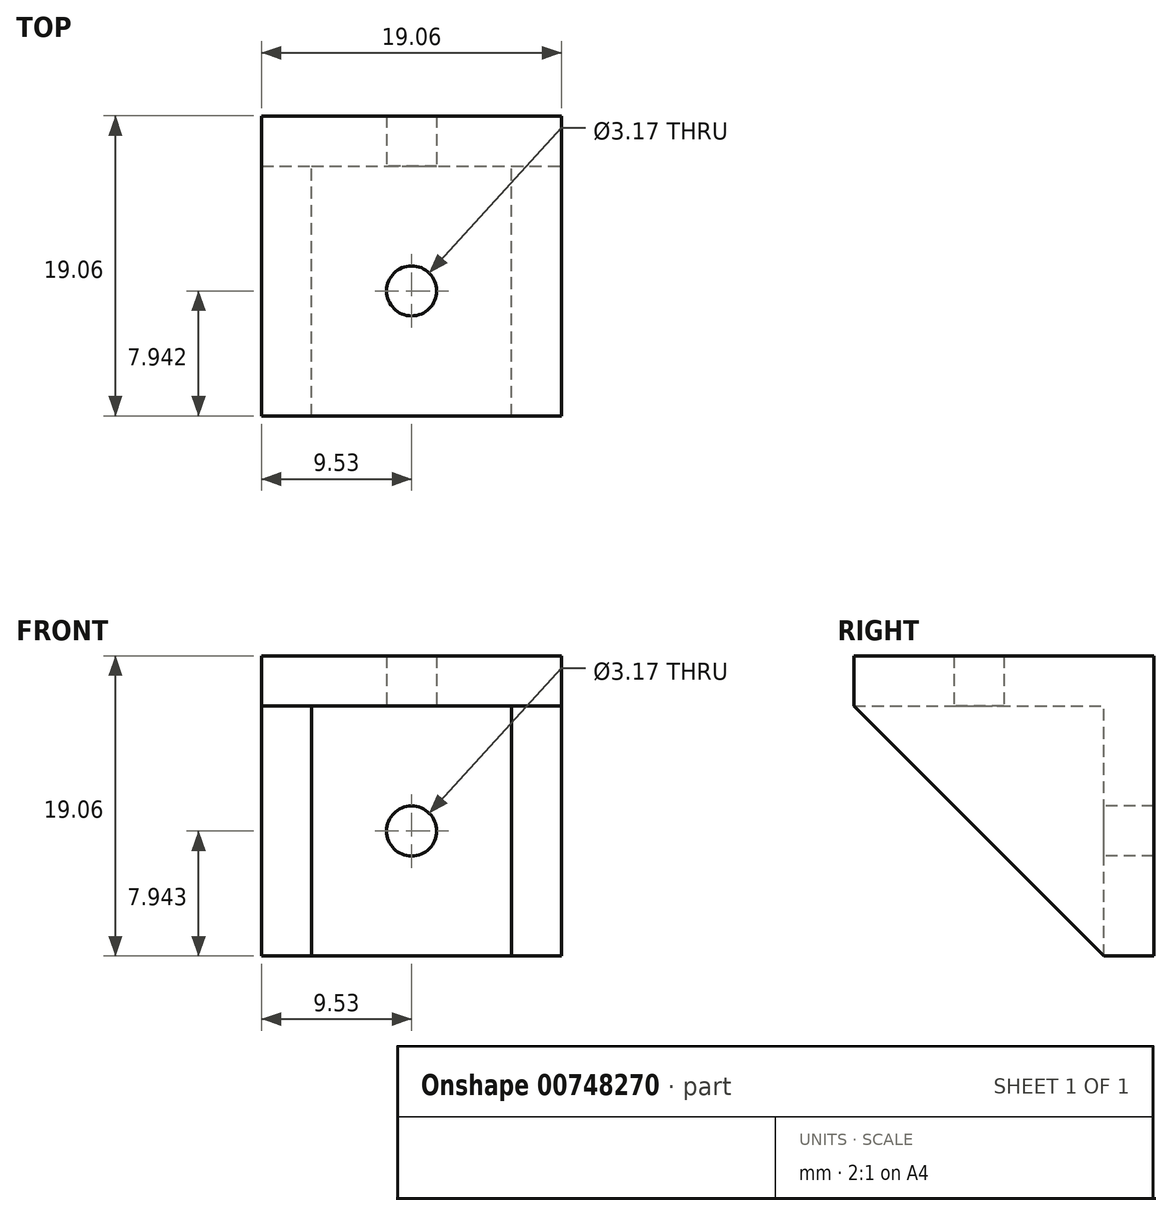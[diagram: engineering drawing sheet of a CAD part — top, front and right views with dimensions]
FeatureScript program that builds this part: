
annotation { "Feature Type Name" : "Feature", "Feature Type Description" : "" }
export const myFeature = defineFeature(function(context is Context, id is Id, definition is map)
    precondition{}
    {
        {
            var Q0;
            Q0=qCreatedBy(makeId("Top.planeOp"),FACE);
            var sketch = newSketch(context, id + "F0", { "sketchPlane" : qUnion([Q0])});
            skLineSegment(sketch, "E0.bottom", {"start": v(9.53, -9.53) * mm, "end": v(-9.53, -9.53) * mm});
            skLineSegment(sketch, "E0.top", {"start": v(9.52, 9.53) * mm, "end": v(-9.52, 9.53) * mm});
            skLineSegment(sketch, "E0.left", {"start": v(9.53, -9.53) * mm, "end": v(9.53, 9.52) * mm});
            skLineSegment(sketch, "E0.right", {"start": v(-9.53, -9.53) * mm, "end": v(-9.53, 9.52) * mm});
            skPoint(sketch, "E0.middle", {"position": v(0, 0) * mm});
            skSolve(sketch);
        }
        {
            var Q0;
            Q0 = qSketchRegion(id + "F0", true);
            extrude(context, id + "F1", {"entities" : qUnion([Q0]), "depth" : 3.17 * mm, "offsetDistance" : 25.4 * mm});
        }
        {
            var Q0;
            Q0=makeQuery(id+"F1.opExtrude","CAP_FACE",FACE,{"disambiguationData":[OSD([sQuery(id+"F0.wireOp",EDGE,"E0.bottom"),sQuery(id+"F0.wireOp",EDGE,"E0.top"),sQuery(id+"F0.wireOp",EDGE,"E0.left"),sQuery(id+"F0.wireOp",EDGE,"E0.right")])],"isStart":true});
            var sketch = newSketch(context, id + "F2", { "sketchPlane" : qUnion([Q0])});
            skLineSegment(sketch, "E1.bottom", {"start": v(-9.53, -9.52) * mm, "end": v(9.53, -9.52) * mm});
            skLineSegment(sketch, "E1.top", {"start": v(-9.53, -6.35) * mm, "end": v(9.53, -6.35) * mm});
            skLineSegment(sketch, "E1.left", {"start": v(-9.53, -9.52) * mm, "end": v(-9.53, -6.35) * mm});
            skLineSegment(sketch, "E1.right", {"start": v(9.53, -9.52) * mm, "end": v(9.53, -6.35) * mm});
            skSolve(sketch);
        }
        {
            var Q0;
            Q0 = qSketchRegion(id + "F2", true);
            extrude(context, id + "F3", {"entities" : qUnion([Q0]), "operationType" : NewBodyOperationType.ADD, "depth" : 15.88 * mm, "offsetDistance" : 25.4 * mm});
        }
        {
            var Q0;
            Q0=makeQuery(id+"F3.boolean.opBoolean","MERGE",FACE,{"derivedFrom":[makeQuery(id+"F1.opExtrude","SWEPT_FACE",FACE,{"disambiguationData":[OSD([sQuery(id+"F0.wireOp",EDGE,"E0.right")])]}),makeQuery(id+"F3.opExtrude","SWEPT_FACE",FACE,{"disambiguationData":[OSD([sQuery(id+"F2.wireOp",EDGE,"E1.left")])]})]});
            var sketch = newSketch(context, id + "F4", { "sketchPlane" : qUnion([Q0])});
            skLineSegment(sketch, "E2", {"start": v(9.53, 0) * mm, "end": v(-6.35, -15.88) * mm});
            skLineSegment(sketch, "E3", {"start": v(-6.35, -15.88) * mm, "end": v(-6.35, 0) * mm});
            skLineSegment(sketch, "E4", {"start": v(-6.35, 0) * mm, "end": v(9.53, 0) * mm});
            skSolve(sketch);
        }
        {
            var Q0;
            Q0 = qSketchRegion(id + "F4", true);
            extrude(context, id + "F5", {"entities" : qUnion([Q0]), "operationType" : NewBodyOperationType.ADD, "oppositeDirection" : true, "depth" : 3.17 * mm, "offsetDistance" : 25.4 * mm});
        }
        {
            var Q0;
            Q0=makeQuery(id+"F3.boolean.opBoolean","MERGE",FACE,{"derivedFrom":[makeQuery(id+"F1.opExtrude","SWEPT_FACE",FACE,{"disambiguationData":[OSD([sQuery(id+"F0.wireOp",EDGE,"E0.left")])]}),makeQuery(id+"F3.opExtrude","SWEPT_FACE",FACE,{"disambiguationData":[OSD([sQuery(id+"F2.wireOp",EDGE,"E1.right")])]})]});
            var sketch = newSketch(context, id + "F6", { "sketchPlane" : qUnion([Q0])});
            skLineSegment(sketch, "E5", {"start": v(6.35, -15.88) * mm, "end": v(-9.53, 0) * mm});
            skLineSegment(sketch, "E6", {"start": v(-9.53, 0) * mm, "end": v(6.35, 0) * mm});
            skLineSegment(sketch, "E7", {"start": v(6.35, 0) * mm, "end": v(6.35, -15.88) * mm});
            skSolve(sketch);
        }
        {
            var Q0;
            Q0 = qSketchRegion(id + "F6", true);
            extrude(context, id + "F7", {"entities" : qUnion([Q0]), "operationType" : NewBodyOperationType.ADD, "oppositeDirection" : true, "depth" : 3.17 * mm, "offsetDistance" : 25.4 * mm});
        }
        {
            var Q0;
            Q0=makeQuery(id+"F3.opExtrude","SWEPT_FACE",FACE,{"disambiguationData":[OSD([sQuery(id+"F2.wireOp",EDGE,"E1.top")])]});
            var sketch = newSketch(context, id + "F8", { "sketchPlane" : qUnion([Q0])});
            skLineSegment(sketch, "E8", {"start": v(6.35, -15.88) * mm, "end": v(-6.35, 0) * mm, "construction": true});
            skLineSegment(sketch, "E9", {"start": v(-6.35, -15.88) * mm, "end": v(6.35, 0) * mm, "construction": true});
            skCircle(sketch, "E10", {"center": v(0, -7.94) * mm, "radius": 1.59 * mm});
            skSolve(sketch);
        }
        {
            var Q0;
            Q0 = qSketchRegion(id + "F8", true);
            extrude(context, id + "F9", {"entities" : qUnion([Q0]), "operationType" : NewBodyOperationType.REMOVE, "endBound" : BoundingType.THROUGH_ALL, "oppositeDirection" : true, "depth" : 25.4 * mm, "offsetDistance" : 25.4 * mm});
        }
        {
            var Q0;
            Q0=makeQuery(id+"F1.opExtrude","CAP_FACE",FACE,{"disambiguationData":[OSD([sQuery(id+"F0.wireOp",EDGE,"E0.bottom"),sQuery(id+"F0.wireOp",EDGE,"E0.top"),sQuery(id+"F0.wireOp",EDGE,"E0.left"),sQuery(id+"F0.wireOp",EDGE,"E0.right")])],"isStart":true});
            var sketch = newSketch(context, id + "F10", { "sketchPlane" : qUnion([Q0])});
            skLineSegment(sketch, "E11", {"start": v(6.35, -6.35) * mm, "end": v(-6.35, 9.53) * mm, "construction": true});
            skCircle(sketch, "E12", {"center": v(0, 1.59) * mm, "radius": 1.59 * mm});
            skSolve(sketch);
        }
        {
            var Q0;
            Q0 = qSketchRegion(id + "F10", true);
            extrude(context, id + "F11", {"entities" : qUnion([Q0]), "operationType" : NewBodyOperationType.REMOVE, "endBound" : BoundingType.THROUGH_ALL, "oppositeDirection" : true, "depth" : 25.4 * mm, "offsetDistance" : 25.4 * mm});
        }
    });
